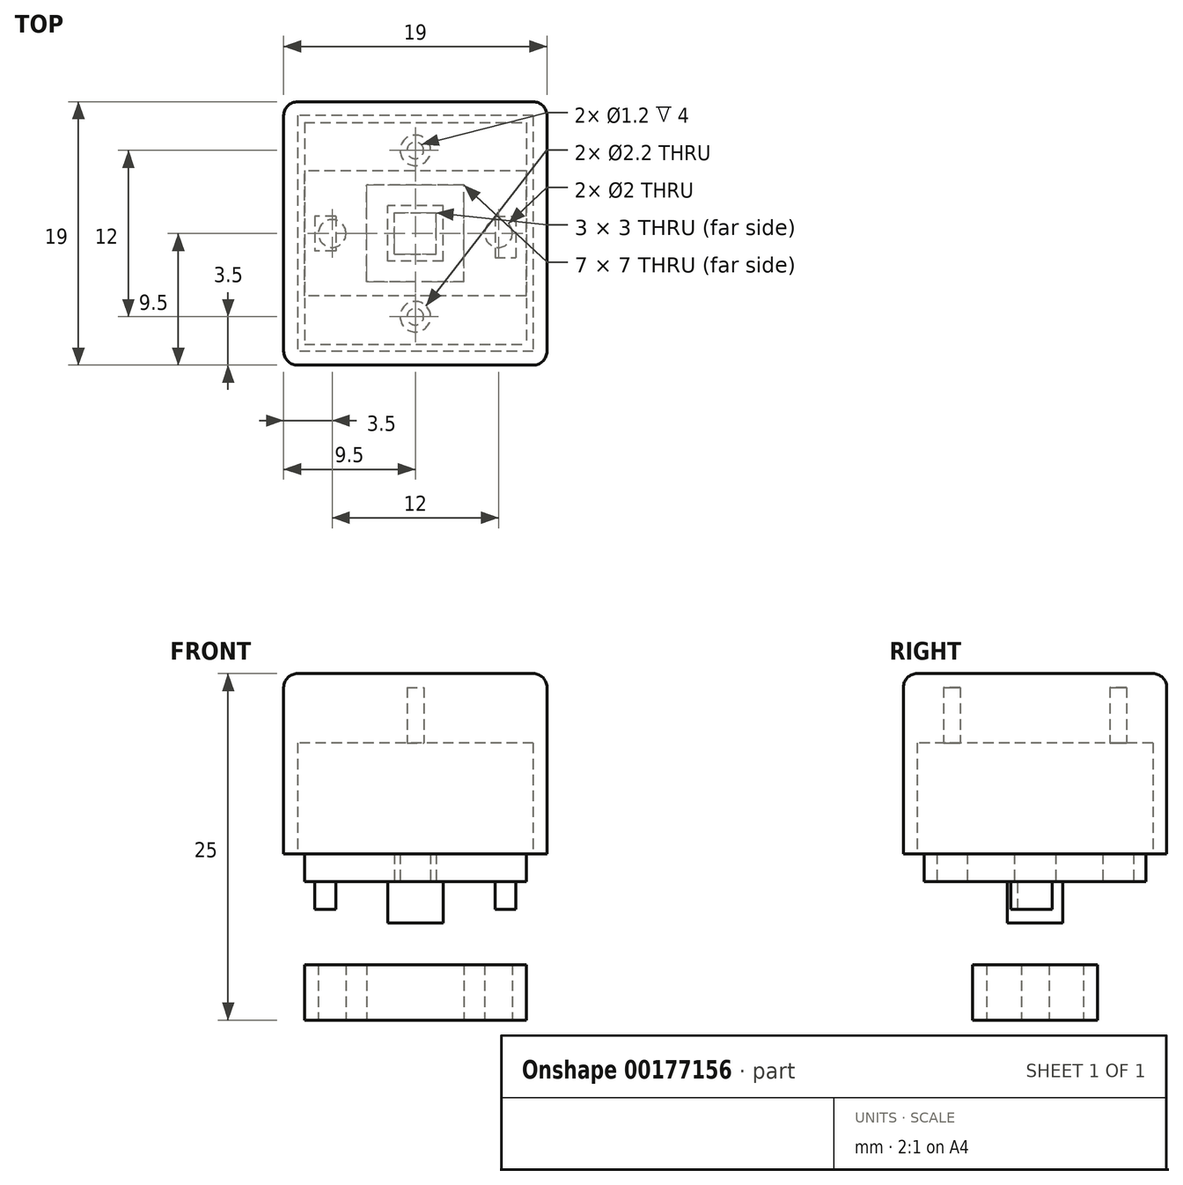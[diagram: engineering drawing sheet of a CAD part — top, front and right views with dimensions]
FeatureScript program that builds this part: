
annotation { "Feature Type Name" : "Feature", "Feature Type Description" : "" }
export const myFeature = defineFeature(function(context is Context, id is Id, definition is map)
    precondition{}
    {
        {
            var Q0;
            Q0=qCreatedBy(makeId("Top.planeOp"),FACE);
            var sketch = newSketch(context, id + "F0", { "sketchPlane" : qUnion([Q0])});
            skLineSegment(sketch, "E0.bottom", {"start": v(3.5, -3.5) * mm, "end": v(-3.5, -3.5) * mm});
            skLineSegment(sketch, "E0.top", {"start": v(3.5, 3.5) * mm, "end": v(-3.5, 3.5) * mm});
            skLineSegment(sketch, "E0.left", {"start": v(3.5, -3.5) * mm, "end": v(3.5, 3.5) * mm});
            skLineSegment(sketch, "E0.right", {"start": v(-3.5, -3.5) * mm, "end": v(-3.5, 3.5) * mm});
            skPoint(sketch, "E0.middle", {"position": v(0, 0) * mm});
            skLineSegment(sketch, "E1.bottom", {"start": v(8, -4.5) * mm, "end": v(-8, -4.5) * mm});
            skLineSegment(sketch, "E1.top", {"start": v(8, 4.5) * mm, "end": v(-8, 4.5) * mm});
            skLineSegment(sketch, "E1.left", {"start": v(8, -4.5) * mm, "end": v(8, 4.5) * mm});
            skLineSegment(sketch, "E1.right", {"start": v(-8, -4.5) * mm, "end": v(-8, 4.5) * mm});
            skCircle(sketch, "E2", {"center": v(-6, 0) * mm, "radius": 1 * mm});
            skCircle(sketch, "E3", {"center": v(6, 0) * mm, "radius": 1 * mm});
            skSolve(sketch);
        }
        {
            var Q0;
            Q0 = qSketchRegion(id + "F0", true);
            extrude(context, id + "F1", {"entities" : qUnion([Q0]), "depth" : 4 * mm});
        }
        {
            var Q0;
            Q0=qCreatedBy(makeId("Top.planeOp"),FACE);
            cPlane(context, id + "F2", {"entities" : qUnion([Q0]), "cplaneType" : CPlaneType.OFFSET, "offset" : 10 * mm, "width" : 150 * mm, "height" : 150 * mm});
        }
        {
            var Q0;
            Q0=qCreatedBy(id+"F2.planeOp",FACE);
            var sketch = newSketch(context, id + "F3", { "sketchPlane" : qUnion([Q0])});
            skLineSegment(sketch, "E4.bottom", {"start": v(2, -2) * mm, "end": v(-2, -2) * mm});
            skLineSegment(sketch, "E4.top", {"start": v(2, 2) * mm, "end": v(-2, 2) * mm});
            skLineSegment(sketch, "E4.left", {"start": v(2, -2) * mm, "end": v(2, 2) * mm});
            skLineSegment(sketch, "E4.right", {"start": v(-2, -2) * mm, "end": v(-2, 2) * mm});
            skPoint(sketch, "E4.middle", {"position": v(0, 0) * mm});
            skSolve(sketch);
        }
        {
            var Q0;
            Q0 = qSketchRegion(id + "F3", true);
            extrude(context, id + "F4", {"entities" : qUnion([Q0]), "oppositeDirection" : true, "depth" : 3 * mm});
        }
        {
            var Q0;
            Q0=qCreatedBy(id+"F2.planeOp",FACE);
            var sketch = newSketch(context, id + "F5", { "sketchPlane" : qUnion([Q0])});
            skLineSegment(sketch, "E5.bottom", {"start": v(8, -8) * mm, "end": v(-8, -8) * mm});
            skLineSegment(sketch, "E5.top", {"start": v(8, 8) * mm, "end": v(-8, 8) * mm});
            skLineSegment(sketch, "E5.left", {"start": v(8, -8) * mm, "end": v(8, 8) * mm});
            skLineSegment(sketch, "E5.right", {"start": v(-8, -8) * mm, "end": v(-8, 8) * mm});
            skPoint(sketch, "E5.middle", {"position": v(0, 0) * mm});
            skCircle(sketch, "E6", {"center": v(0, -6) * mm, "radius": 1.1 * mm});
            skCircle(sketch, "E7", {"center": v(0, 6) * mm, "radius": 1.1 * mm});
            skLineSegment(sketch, "E8.bottom", {"start": v(1.5, 1.5) * mm, "end": v(-1.5, 1.5) * mm});
            skLineSegment(sketch, "E8.top", {"start": v(1.5, -1.5) * mm, "end": v(-1.5, -1.5) * mm});
            skLineSegment(sketch, "E8.left", {"start": v(1.5, 1.5) * mm, "end": v(1.5, -1.5) * mm});
            skLineSegment(sketch, "E8.right", {"start": v(-1.5, 1.5) * mm, "end": v(-1.5, -1.5) * mm});
            skSolve(sketch);
        }
        {
            var Q0;
            Q0 = qSketchRegion(id + "F5", true);
            extrude(context, id + "F6", {"entities" : qUnion([Q0]), "depth" : 3 * mm});
        }
        {
            var Q0;
            Q0=qCreatedBy(makeId("Top.planeOp"),FACE);
            cPlane(context, id + "F7", {"entities" : qUnion([Q0]), "cplaneType" : CPlaneType.OFFSET, "offset" : 12 * mm, "width" : 150 * mm, "height" : 150 * mm});
        }
        {
            var Q0;
            Q0=qCreatedBy(id+"F7.planeOp",FACE);
            var sketch = newSketch(context, id + "F8", { "sketchPlane" : qUnion([Q0])});
            skLineSegment(sketch, "E9.bottom", {"start": v(9.5, -9.5) * mm, "end": v(-9.5, -9.5) * mm});
            skLineSegment(sketch, "E9.top", {"start": v(9.5, 9.5) * mm, "end": v(-9.5, 9.5) * mm});
            skLineSegment(sketch, "E9.left", {"start": v(9.5, -9.5) * mm, "end": v(9.5, 9.5) * mm});
            skLineSegment(sketch, "E9.right", {"start": v(-9.5, -9.5) * mm, "end": v(-9.5, 9.5) * mm});
            skPoint(sketch, "E9.middle", {"position": v(0, 0) * mm});
            skSolve(sketch);
        }
        {
            var Q0;
            Q0 = qSketchRegion(id + "F8", true);
            extrude(context, id + "F9", {"entities" : qUnion([Q0]), "depth" : 13 * mm});
        }
        {
            var Q0;
            Q0=makeQuery(id+"F9.opExtrude","CAP_FACE",FACE,{"disambiguationData":[OSD([sQuery(id+"F8.wireOp",EDGE,"E9.bottom"),sQuery(id+"F8.wireOp",EDGE,"E9.top"),sQuery(id+"F8.wireOp",EDGE,"E9.left"),sQuery(id+"F8.wireOp",EDGE,"E9.right")])],"isStart":true});
            var sketch = newSketch(context, id + "F10", { "sketchPlane" : qUnion([Q0])});
            skLineSegment(sketch, "E10.bottom", {"start": v(8.5, -8.5) * mm, "end": v(-8.5, -8.5) * mm});
            skLineSegment(sketch, "E10.top", {"start": v(8.5, 8.5) * mm, "end": v(-8.5, 8.5) * mm});
            skLineSegment(sketch, "E10.left", {"start": v(8.5, -8.5) * mm, "end": v(8.5, 8.5) * mm});
            skLineSegment(sketch, "E10.right", {"start": v(-8.5, -8.5) * mm, "end": v(-8.5, 8.5) * mm});
            skPoint(sketch, "E10.middle", {"position": v(0, 0) * mm});
            skSolve(sketch);
        }
        {
            var Q0;
            Q0 = qSketchRegion(id + "F10", true);
            extrude(context, id + "F11", {"entities" : qUnion([Q0]), "operationType" : NewBodyOperationType.REMOVE, "oppositeDirection" : true, "depth" : 8 * mm});
        }
        {
            var Q0;
            Q0=makeQuery(id+"F11.boolean.opBoolean","COPY",FACE,{"derivedFrom":makeQuery(id+"F11.opExtrude","CAP_FACE",FACE,{"disambiguationData":[OSD([sQuery(id+"F10.wireOp",EDGE,"E10.bottom"),sQuery(id+"F10.wireOp",EDGE,"E10.top"),sQuery(id+"F10.wireOp",EDGE,"E10.left"),sQuery(id+"F10.wireOp",EDGE,"E10.right")])],"isStart":false})});
            var sketch = newSketch(context, id + "F12", { "sketchPlane" : qUnion([Q0])});
            skCircle(sketch, "E11", {"center": v(0, 6) * mm, "radius": 0.6 * mm});
            skCircle(sketch, "E12", {"center": v(0, -6) * mm, "radius": 0.6 * mm});
            skSolve(sketch);
        }
        {
            var Q0;
            Q0 = qSketchRegion(id + "F12", true);
            extrude(context, id + "F13", {"entities" : qUnion([Q0]), "operationType" : NewBodyOperationType.REMOVE, "oppositeDirection" : true, "depth" : 4 * mm});
        }
        {
            var Q0;
            Q0=makeQuery(id+"F9.opExtrude","SWEPT_EDGE",EDGE,{"disambiguationData":[OSD([sQuery(id+"F8.wireOp",EDGE,"E9.bottom"),sQuery(id+"F8.wireOp",EDGE,"E9.right")])]});
            var Q1;
            Q1=makeQuery(id+"F9.opExtrude","SWEPT_EDGE",EDGE,{"disambiguationData":[OSD([sQuery(id+"F8.wireOp",EDGE,"E9.bottom"),sQuery(id+"F8.wireOp",EDGE,"E9.left")])]});
            var Q2;
            Q2=makeQuery(id+"F9.opExtrude","SWEPT_EDGE",EDGE,{"disambiguationData":[OSD([sQuery(id+"F8.wireOp",EDGE,"E9.top"),sQuery(id+"F8.wireOp",EDGE,"E9.right")])]});
            var Q3;
            Q3=makeQuery(id+"F9.opExtrude","SWEPT_EDGE",EDGE,{"disambiguationData":[OSD([sQuery(id+"F8.wireOp",EDGE,"E9.top"),sQuery(id+"F8.wireOp",EDGE,"E9.left")])]});
            var Q4;
            Q4=makeQuery(id+"F9.opExtrude","CAP_FACE",FACE,{"disambiguationData":[OSD([sQuery(id+"F8.wireOp",EDGE,"E9.bottom"),sQuery(id+"F8.wireOp",EDGE,"E9.top"),sQuery(id+"F8.wireOp",EDGE,"E9.left"),sQuery(id+"F8.wireOp",EDGE,"E9.right")])],"isStart":false});
            fillet(context, id + "F14", {"entities" : qUnion([Q0, Q1, Q2, Q3, Q4]), "radius" : 1 * mm, "tangentPropagation" : true, "allowEdgeOverflow" : false});
        }
        {
            var Q0;
            Q0=makeQuery(id+"F6.opExtrude","CAP_FACE",FACE,{"disambiguationData":[OSD([sQuery(id+"F5.wireOp",EDGE,"E5.bottom"),sQuery(id+"F5.wireOp",EDGE,"E5.top"),sQuery(id+"F5.wireOp",EDGE,"E5.left"),sQuery(id+"F5.wireOp",EDGE,"E5.right"),sQuery(id+"F5.wireOp",EDGE,"E6"),sQuery(id+"F5.wireOp",EDGE,"E7")])],"isStart":true});
            var sketch = newSketch(context, id + "F15", { "sketchPlane" : qUnion([Q0])});
            skLineSegment(sketch, "E13.bottom", {"start": v(5.75, -1.25) * mm, "end": v(7.25, -1.25) * mm});
            skLineSegment(sketch, "E13.top", {"start": v(5.75, 1.75) * mm, "end": v(7.25, 1.75) * mm});
            skLineSegment(sketch, "E13.left", {"start": v(5.75, -1.25) * mm, "end": v(5.75, 1.75) * mm});
            skLineSegment(sketch, "E13.right", {"start": v(7.25, -1.25) * mm, "end": v(7.25, 1.75) * mm});
            skPoint(sketch, "E13.middle", {"position": v(6.5, 0.25) * mm});
            skLineSegment(sketch, "E14.bottom", {"start": v(-5.75, -1.25) * mm, "end": v(-7.25, -1.25) * mm});
            skLineSegment(sketch, "E14.top", {"start": v(-5.75, 1.25) * mm, "end": v(-7.25, 1.25) * mm});
            skLineSegment(sketch, "E14.left", {"start": v(-5.75, -1.25) * mm, "end": v(-5.75, 1.25) * mm});
            skLineSegment(sketch, "E14.right", {"start": v(-7.25, -1.25) * mm, "end": v(-7.25, 1.25) * mm});
            skPoint(sketch, "E14.middle", {"position": v(-6.5, 0) * mm});
            skPoint(sketch, "E14.middle.positionSnap0", {"position": v(-1.5, 0) * mm});
            skPoint(sketch, "E14.cornerSnap0", {"position": v(6.5, -1.25) * mm});
            skPoint(sketch, "E14.centerSnap0", {"position": v(-1.5, 0) * mm});
            skSolve(sketch);
        }
        {
            var Q0;
            Q0 = qSketchRegion(id + "F15", true);
            extrude(context, id + "F16", {"entities" : qUnion([Q0]), "operationType" : NewBodyOperationType.ADD, "depth" : 2 * mm});
        }
    });
